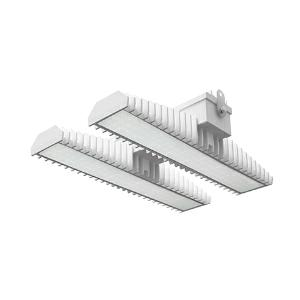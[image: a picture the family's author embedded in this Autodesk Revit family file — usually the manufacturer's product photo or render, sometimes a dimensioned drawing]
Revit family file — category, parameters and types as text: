
# Revit family: 3f_filippi_-_3f_lem_medio_3f_filippi_-_58893_a0812_-_3f_lem_2_led_100_cr_medio___vs_26e0
name_source: partatom
category: Lighting Fixtures
units: mm (PartAtom-declared; Revit-internal decimal feet)

## family parameters
Cut with Voids When Loaded = No
Host = Face
Light Source = No
Part Type = Normal
Room Calculation Point = No
Round Connector Dimension = Use Diameter
Shared = No

## types (1)
- 3F Filippi - 3F LEM Medio (1 x LED, 13466 lm, 109 W, 4000 K)
    Apparent Load = 109 VA
    Approval mark = CE
    CIE Flux Codes = 77 92 98 100 100
    Color Rendering = 80
    Color Temperature = 4000 K
    Control Gear = Electronic ballast
    Default Elevation = 1800 mm
    Description = Industrial luminaire with high light output and high luminous efficiency designed with the most innovative technologies for environments with temperature up to 55°C.

ILLUMINOTECHNICAL
Luminous efficiency 100% (DLOR 98%, ULOR 2%).
Initial luminous flux of the luminaire 13466 lm.
Medium distribution with rectangular shape.
Installation Interdistance Transv.D = 1.10 x hu - Long.D = 1.14 x hu.
Tabular UGR (CIE 117 - 4H-8H; S=0.25H; 70/50/20): RUG 20.5 - 20.4.
Beam angle: 58° - 57°.
Luminous efficacy 124 lm/W.
Lifetime (L93/B10): 30000 h. (tq+25°C)
Lifetime (L90/B10): 50000 h. (tq+25°C)
Lifetime (L85/B10): 80000 h. (tq+25°C)
Lifetime (L80/B10): 100000 h. (tq+25°C)
Lifetime (L85/B10): 50000 h. (tq+55°C)
Sudden decreased luminous flux after 50000 hours: 0% (C0).
Photobiological safety in compliance with IEC/TR 62778: RG0 risk exempt, (IEC 62471).
In compliance with IEC/EN 62722-2-1 - IEC/EN 62717 standards.

SOURCE
2 Mid-Power linear LED modules 50W/840.
Energy efficiency class (UE 2019/2020 - UE 2019/2015): C.
CIE 13.3 Colour rendering index: CRI >80 (R9 <50%).
IES TM-30 Fidelity Index: Rf = 84 Rg = 95.
CCT nominal colour temperature 4000 K.
Colour initial tolerance (MacAdam): SDCM 3.

MECHANICAL
Passive modular heatsinks in die-casted aluminium, painted in white colour.
To optimize the thermal management of the LED module, the heatsinks are oversized and provided with self-cleaning of cooling fins.
Wiring body in aluminium and galvanised steel anchored solidly to the sinks and thermally separated.
3F Lens lenses with high luminous efficiency, transparent methacrylate (PMMA), fixed to the LED modules.
Fixing brackets in stainless steel.
Luminaire with limited surface temperature. - D - (EN 60598-2-24)
Dimensions: 470x542 mm, height 133 mm. Weight 10.1 kg.
IP65 protection degree.
Mechanical strength to impacts IK06 (1 joule).
Glow-wire test resistance 650°C.

ELECTRICAL
Halogen Free electronic wiring 230V-50/60Hz, power factor 0.97, THD <25%, constant output current, class I, 1 driver.
Power of the luminaire 109 W.
ENEC - CE.
SAFE FLICKER: PstLM=<1 and SVM=<0.4 (IEC TR 61547-1 and IEC TR 63158), to ensure a more comfortable and safe light.
Luminaire compliant with EN 60598-2-22 for power supply from a centralised emergency system CPSS (Central Power Supply System), not incorporated in the luminaire - high risk areas excluded. The default power and flux are 100% in AC and 100% in DC.
Ambient temperature from -30°C to +55°C.
Temperature class T6 max 85°C.
Quick connection via M20 3P connector with 9-13 mm tightening range.
Power unit positioned on a separate compartment by the LED module to ensure optimum temperatures of cabling components, to be inspectable and maintainable.
Relative humidity UR: <85%.

INSTALLATION
Ceiling / Suspended / Wall.
All accessories dedicated to this product are available on the Catalog and on our website www.3F-Filippi.com.

ACCESSORIES
A0812 - Anti-glare microprismatic VS moulded glass, tempered, not flammable, with sealing gasket.
One required for each light module. The pack contains 10 pieces.

APPLICATIONS
In commercial environments, exhibition and industrial areas, stores, open areas.
Applications with high ambient temperature up to 55°C.
Environments in which it is necessary a total protection against falling fragments (eg environments with foodstuffs or machines with moving parts or with extreme temperature changes), use luminaires with polycarbonate lenses.

WARNING
Fixture not suitable for cold stores with an ambient temperature <0°C and/or relative humidity >85%.
Luminaire designed for disposal/recycling at end-of-life.
Replaceable (LED only) light source by a professional. Replaceable control gear by a professional.
    Height = 133 mm
    Lamp = 1 x LED
    Lamp Light Flux = 13466 lm
    Lamp Power = 109 W
    Lamp count = 1
    Length = 470 mm
    Lifetime = 50000 h
    Luminous efficacy = 124 lm/W
    Manufacturer = 3F Filippi
    ModVariant = No
    Model = 3F Filippi - 58893+A0812 - 3F LEM 2 LED 100 CR MEDIO + VS
    Mounting Place = Ceiling
    Mounting Type = Pendant
    Number of Poles = 1
    OnlyDefault = Yes
    Power Factor = 1
    Product Name = 3F Filippi - 3F LEM Medio
    Product group = pendant luminaire
    ProductGroupID = 9
    Protection Class = Protection class I
    Protection Degree = IP 65
    RLX_Detail_Level = 1
    RLX_Emergency_Light_Flux = 0 lm
    RLX_Emergency_Type = 0
    RLX_Emergency_Type_DB = No
    RlxData = <blob elided: 95237 chars, md5=d0c83f87>
    Socket = socket
    Standby Power = 0 W
    System Light Flux = 13466 lm
    System Power = 109 W
    Type Comments = Product without accessories
    Type Image = 3f_filippi_-_lem_2__a0812.jpg
    URL = http://relux.com
    VarID = ---
    Voltage = 0 V
    Weight = 0.00 kg
    Width = 542 mm

## geometry (parser evidence)
native form markers: Blend x4, Sweep x11
no freeform markers — native parametric forms only
